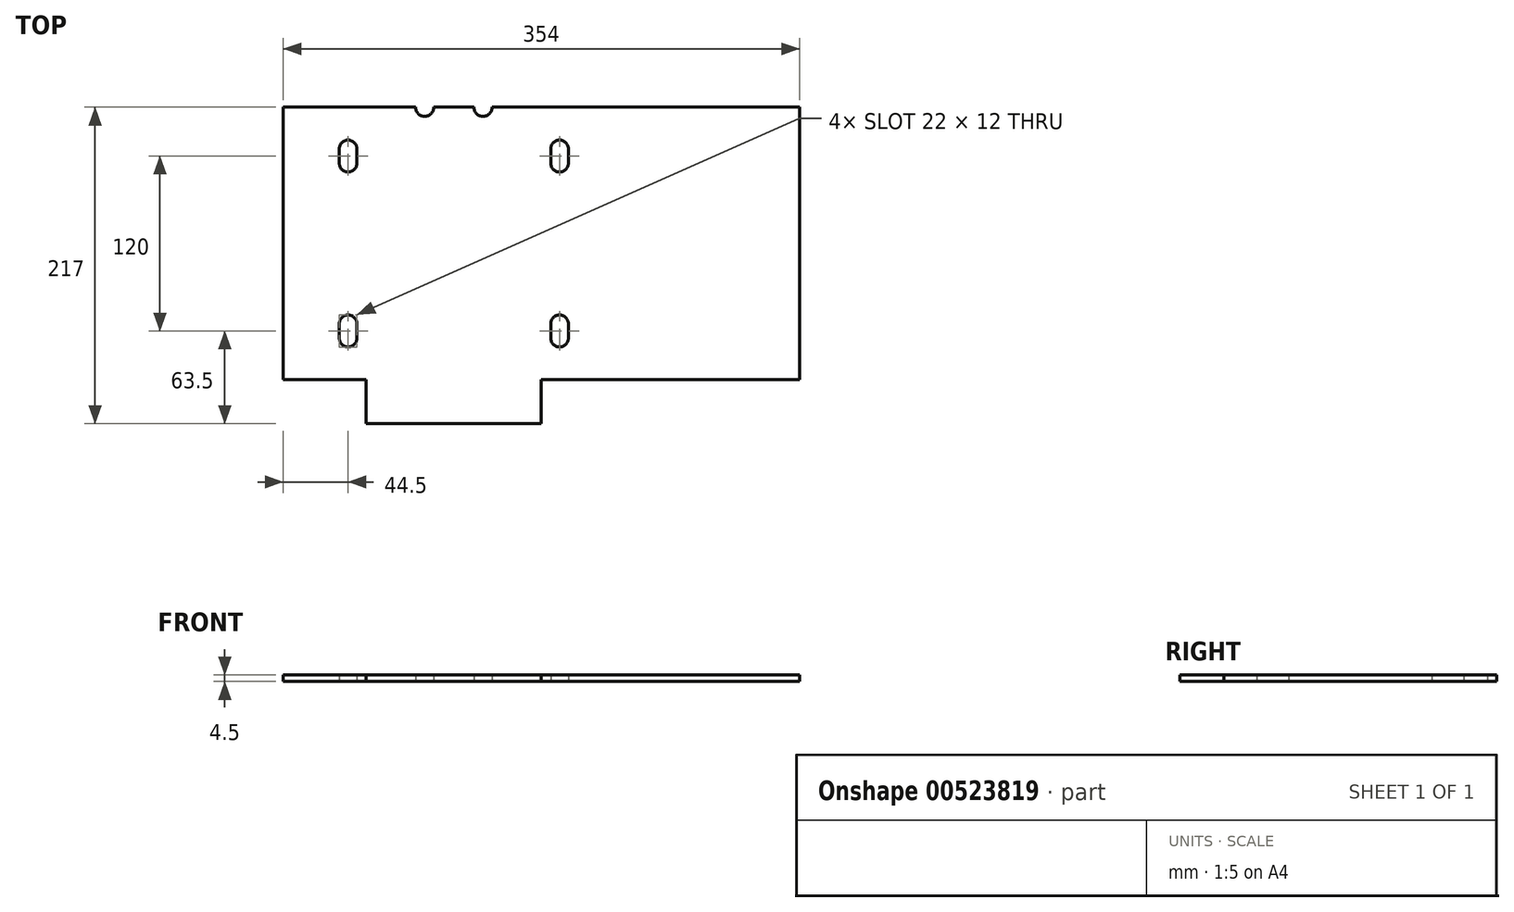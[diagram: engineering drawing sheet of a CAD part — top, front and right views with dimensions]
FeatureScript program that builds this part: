
annotation { "Feature Type Name" : "Feature", "Feature Type Description" : "" }
export const myFeature = defineFeature(function(context is Context, id is Id, definition is map)
    precondition{}
    {
        {
            var Q0;
            Q0=qCreatedBy(makeId("Top.planeOp"),FACE);
            var sketch = newSketch(context, id + "F0", { "sketchPlane" : qUnion([Q0])});
            skLineSegment(sketch, "E0.left", {"start": v(0, 0) * mm, "end": v(0, 187) * mm});
            skLineSegment(sketch, "E0.right", {"start": v(234, 0) * mm, "end": v(234, 187) * mm});
            skLineSegment(sketch, "E1", {"start": v(57, 0) * mm, "end": v(57, -30) * mm});
            skLineSegment(sketch, "E2", {"start": v(57, -30) * mm, "end": v(177, -30) * mm});
            skLineSegment(sketch, "E3", {"start": v(177, -30) * mm, "end": v(177, 0) * mm});
            skLineSegment(sketch, "E4", {"start": v(0, 0) * mm, "end": v(57, 0) * mm});
            skLineSegment(sketch, "E5", {"start": v(177, 0) * mm, "end": v(234, 0) * mm});
            skCircle(sketch, "E6", {"center": v(44.5, 148.5) * mm, "radius": 6 * mm});
            skCircle(sketch, "E7", {"center": v(189.5, 148.5) * mm, "radius": 6 * mm});
            skCircle(sketch, "E8", {"center": v(44.5, 28.5) * mm, "radius": 6 * mm});
            skCircle(sketch, "E9", {"center": v(189.5, 28.5) * mm, "radius": 6 * mm});
            skLineSegment(sketch, "E10", {"start": v(0, 187) * mm, "end": v(117, 93.5) * mm, "construction": true});
            skLineSegment(sketch, "E11", {"start": v(117, 93.5) * mm, "end": v(234, 0) * mm, "construction": true});
            skLineSegment(sketch, "E12", {"start": v(0, 187) * mm, "end": v(234, 187) * mm});
            skCircle(sketch, "E13", {"center": v(97, 187) * mm, "radius": 6.26 * mm});
            skCircle(sketch, "E14", {"center": v(137, 187) * mm, "radius": 6.26 * mm});
            skLineSegment(sketch, "E15", {"start": v(117, 187) * mm, "end": v(117, -30) * mm, "construction": true});
            skCircle(sketch, "E16.0.1.0", {"center": v(44.5, 38.5) * mm, "radius": 6 * mm});
            skCircle(sketch, "E16.0.1.1", {"center": v(189.5, 38.5) * mm, "radius": 6 * mm});
            skCircle(sketch, "E16.0.1.2", {"center": v(44.5, 158.5) * mm, "radius": 6 * mm});
            skCircle(sketch, "E16.0.1.3", {"center": v(189.5, 158.5) * mm, "radius": 6 * mm});
            skLineSegment(sketch, "E16.direction1", {"start": v(44.5, 28.5) * mm, "end": v(69.5, 28.5) * mm, "construction": true});
            skLineSegment(sketch, "E16.direction2", {"start": v(44.5, 28.5) * mm, "end": v(44.5, 38.5) * mm, "construction": true});
            skLineSegment(sketch, "E17", {"start": v(50.5, 38.5) * mm, "end": v(50.5, 28.5) * mm});
            skLineSegment(sketch, "E18", {"start": v(38.5, 38.5) * mm, "end": v(38.5, 28.5) * mm});
            skLineSegment(sketch, "E19", {"start": v(183.5, 38.5) * mm, "end": v(183.5, 28.5) * mm});
            skLineSegment(sketch, "E20", {"start": v(195.5, 38.5) * mm, "end": v(195.5, 28.5) * mm});
            skLineSegment(sketch, "E21", {"start": v(38.5, 158.5) * mm, "end": v(38.5, 148.5) * mm});
            skLineSegment(sketch, "E22", {"start": v(50.5, 158.5) * mm, "end": v(50.5, 148.5) * mm});
            skLineSegment(sketch, "E23", {"start": v(183.5, 158.5) * mm, "end": v(183.5, 148.5) * mm});
            skLineSegment(sketch, "E24", {"start": v(195.5, 158.5) * mm, "end": v(195.5, 148.5) * mm});
            skLineSegment(sketch, "E25", {"start": v(189.5, 158.5) * mm, "end": v(189.5, 148.5) * mm, "construction": true});
            skLineSegment(sketch, "E26", {"start": v(189.5, 153.5) * mm, "end": v(44.5, 33.5) * mm, "construction": true});
            skSolve(sketch);
        }
        {
            var Q0;
            Q0=makeQuery(id+"F0.imprint","IMPRINT",FACE,{"disambiguationData":[TD([[makeQuery(id+"F0.imprint","IMPRINT",EDGE,{"derivedFrom":sQuery(id+"F0.wireOp",EDGE,"E0.left")}),-1.0]])]});
            extrude(context, id + "F1", {"entities" : qUnion([Q0]), "depth" : 4.5 * mm, "offsetDistance" : 25 * mm});
        }
        {
            var Q0;
            Q0=qCreatedBy(makeId("Top.planeOp"),FACE);
            var sketch = newSketch(context, id + "F2", { "sketchPlane" : qUnion([Q0])});
            skLineSegment(sketch, "E27.bottom", {"start": v(234, 0) * mm, "end": v(354, 0) * mm});
            skLineSegment(sketch, "E27.top", {"start": v(234, 187) * mm, "end": v(354, 187) * mm});
            skLineSegment(sketch, "E27.left", {"start": v(234, 0) * mm, "end": v(234, 187) * mm});
            skLineSegment(sketch, "E27.right", {"start": v(354, 0) * mm, "end": v(354, 187) * mm});
            skSolve(sketch);
        }
        {
            var Q0;
            Q0 = qSketchRegion(id + "F2", true);
            extrude(context, id + "F3", {"entities" : qUnion([Q0]), "operationType" : NewBodyOperationType.ADD, "depth" : 4.5 * mm, "offsetDistance" : 25 * mm});
        }
    });
